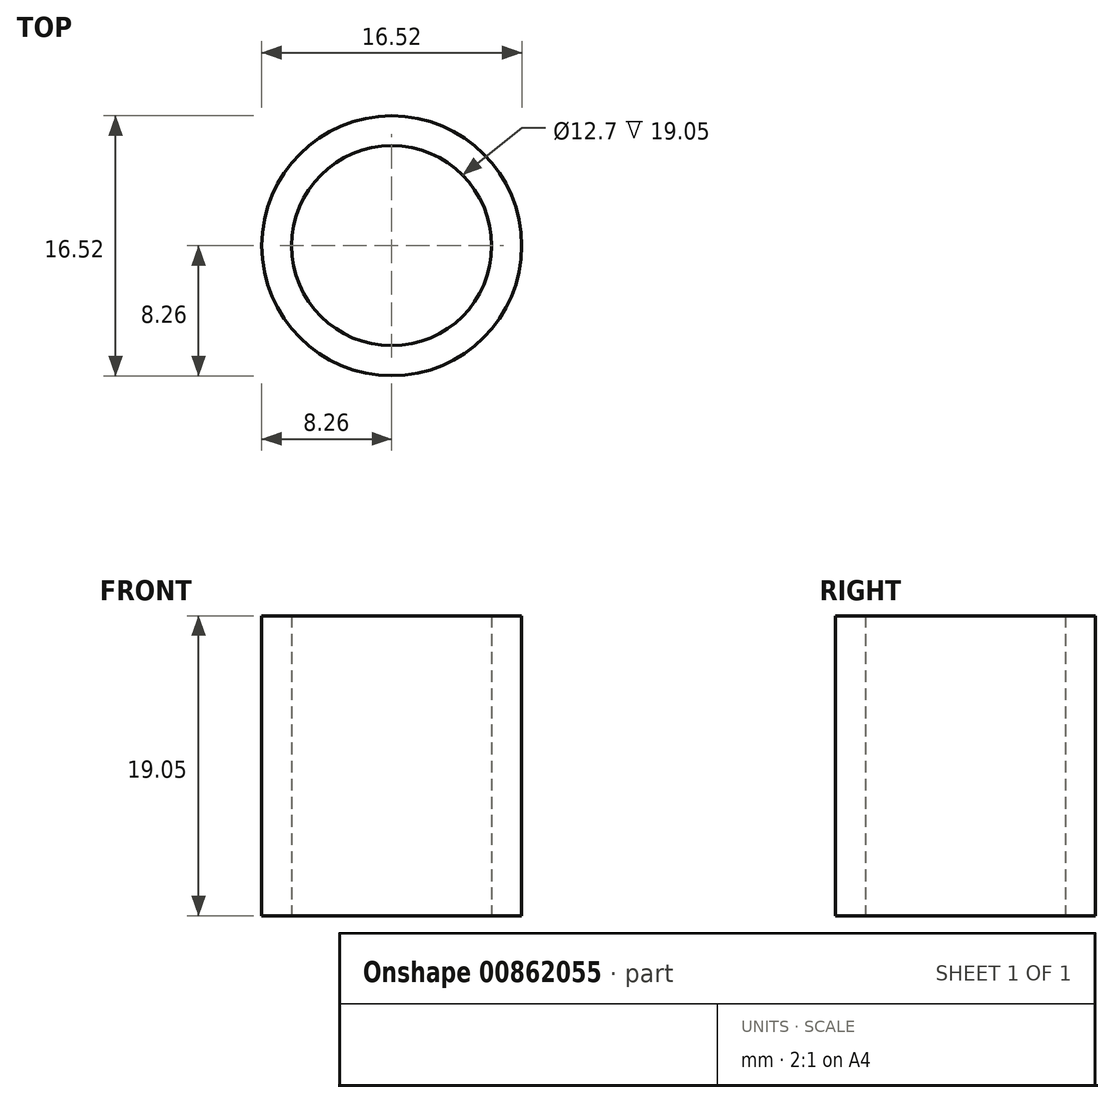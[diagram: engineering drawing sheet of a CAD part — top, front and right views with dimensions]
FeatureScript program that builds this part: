
annotation { "Feature Type Name" : "Feature", "Feature Type Description" : "" }
export const myFeature = defineFeature(function(context is Context, id is Id, definition is map)
    precondition{}
    {
        {
            var Q0;
            Q0=qCreatedBy(makeId("Top.planeOp"),FACE);
            var sketch = newSketch(context, id + "F0", { "sketchPlane" : qUnion([Q0])});
            skCircle(sketch, "E0", {"center": v(0, 0) * mm, "radius": 8.26 * mm});
            skCircle(sketch, "E1", {"center": v(0, 0) * mm, "radius": 6.35 * mm});
            skSolve(sketch);
        }
        {
            var Q0;
            Q0=makeQuery(id+"F0.imprint","IMPRINT",FACE,{"disambiguationData":[TD([[makeQuery(id+"F0.imprint","IMPRINT",EDGE,{"derivedFrom":sQuery(id+"F0.wireOp",EDGE,"E0")}),1.0]])]});
            extrude(context, id + "F1", {"entities" : qUnion([Q0]), "depth" : 19.05 * mm, "offsetDistance" : 25.4 * mm});
        }
    });
